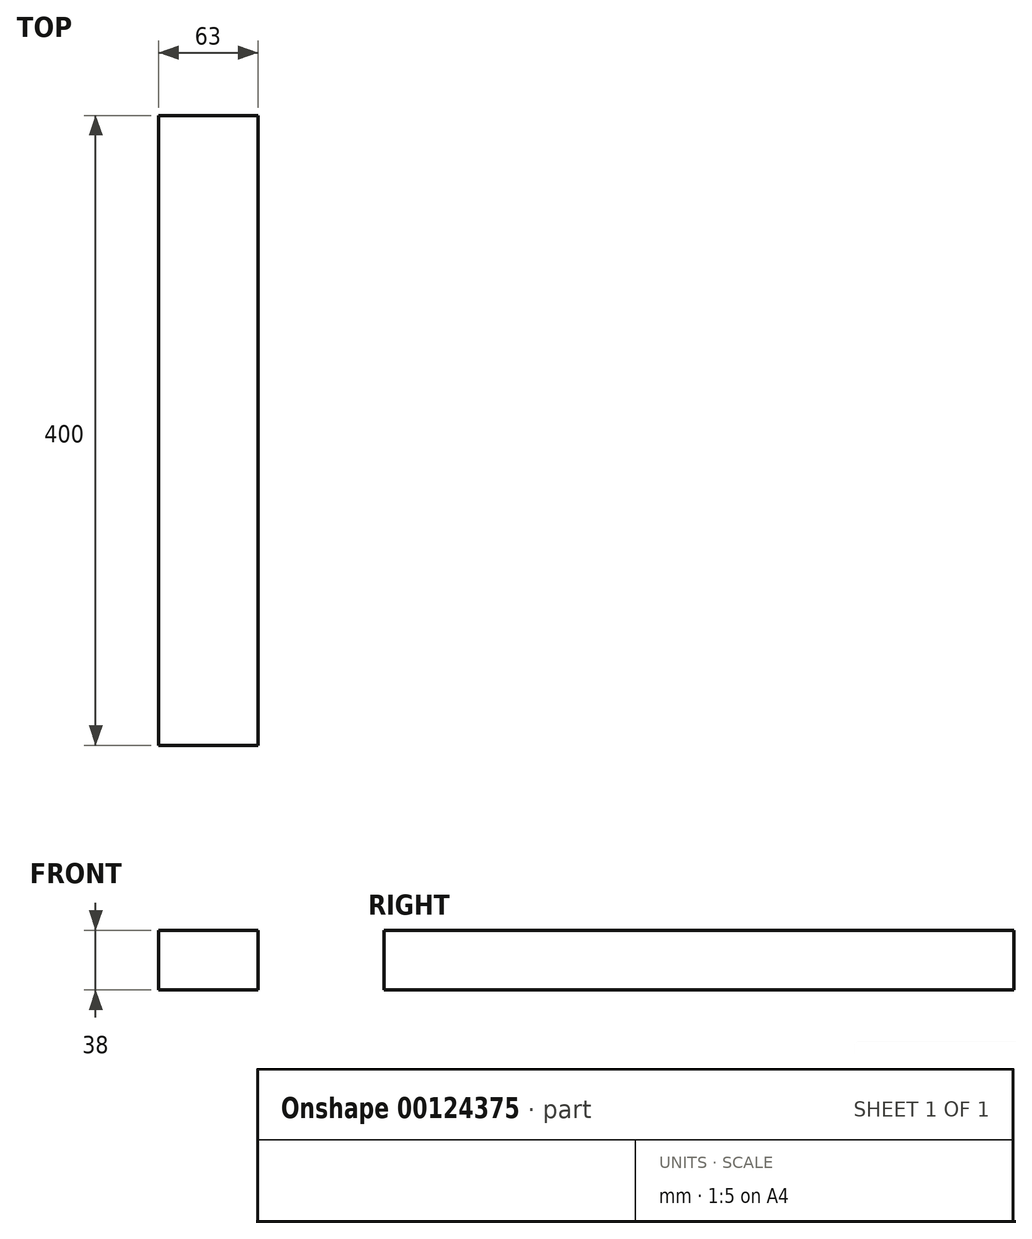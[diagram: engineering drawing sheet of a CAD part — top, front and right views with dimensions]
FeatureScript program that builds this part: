
annotation { "Feature Type Name" : "Feature", "Feature Type Description" : "" }
export const myFeature = defineFeature(function(context is Context, id is Id, definition is map)
    precondition{}
    {
        {
            var Q0;
            Q0=qCreatedBy(makeId("Front.planeOp"),FACE);
            var sketch = newSketch(context, id + "F0", { "sketchPlane" : qUnion([Q0])});
            skLineSegment(sketch, "E0.bottom", {"start": v(31.5, 19) * mm, "end": v(-31.5, 19) * mm});
            skLineSegment(sketch, "E0.top", {"start": v(31.5, -19) * mm, "end": v(-31.5, -19) * mm});
            skLineSegment(sketch, "E0.left", {"start": v(31.5, 19) * mm, "end": v(31.5, -19) * mm});
            skLineSegment(sketch, "E0.right", {"start": v(-31.5, 19) * mm, "end": v(-31.5, -19) * mm});
            skPoint(sketch, "E0.middle", {"position": v(0, 0) * mm});
            skSolve(sketch);
        }
        {
            var Q0;
            Q0 = qSketchRegion(id + "F0", true);
            extrude(context, id + "F1", {"entities" : qUnion([Q0]), "endBound" : BoundingType.SYMMETRIC, "depth" : 400 * mm});
        }
    });
